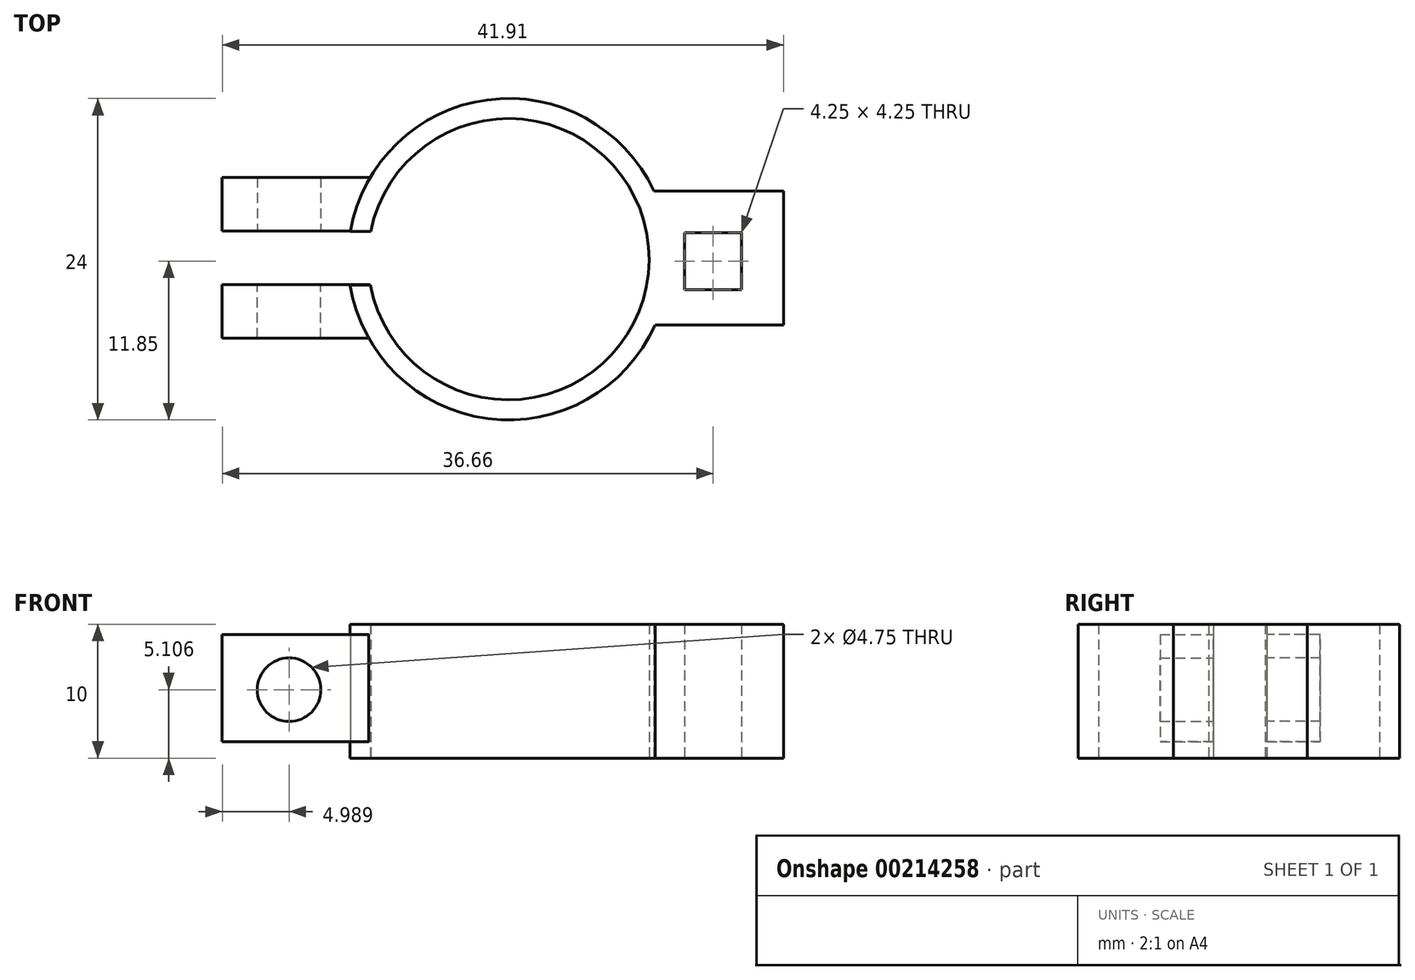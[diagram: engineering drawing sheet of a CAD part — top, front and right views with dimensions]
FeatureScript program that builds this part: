
annotation { "Feature Type Name" : "Feature", "Feature Type Description" : "" }
export const myFeature = defineFeature(function(context is Context, id is Id, definition is map)
    precondition{}
    {
        {
            var Q0;
            Q0=qCreatedBy(makeId("Top.planeOp"),FACE);
            var sketch = newSketch(context, id + "F0", { "sketchPlane" : qUnion([Q0])});
            skLineSegment(sketch, "E0.bottom", {"start": v(7.35, 1.88) * mm, "end": v(3.1, 1.88) * mm});
            skLineSegment(sketch, "E0.top", {"start": v(7.36, -2.38) * mm, "end": v(3.1, -2.38) * mm});
            skLineSegment(sketch, "E0.left", {"start": v(7.35, 1.88) * mm, "end": v(7.36, -2.37) * mm});
            skLineSegment(sketch, "E0.right", {"start": v(3.1, 1.88) * mm, "end": v(3.1, -2.38) * mm});
            skPoint(sketch, "E0.middle", {"position": v(0, 0) * mm});
            skLineSegment(sketch, "E1.bottom", {"start": v(10.48, 5) * mm, "end": v(0.48, 5) * mm});
            skLineSegment(sketch, "E1.top", {"start": v(10.48, -5) * mm, "end": v(0.48, -5) * mm});
            skLineSegment(sketch, "E1.left", {"start": v(10.48, 5) * mm, "end": v(10.48, -5) * mm});
            skLineSegment(sketch, "E1.right", {"start": v(0.48, 5) * mm, "end": v(0.48, -5) * mm});
            skCircle(sketch, "E2", {"center": v(-10.05, -0.1) * mm, "radius": 10.5 * mm});
            skPoint(sketch, "E2.first.point", {"position": v(-2, 6.7) * mm});
            skPoint(sketch, "E2.second.point", {"position": v(-17, 0) * mm});
            skPoint(sketch, "E2.second.point.positionSnap0", {"position": v(-5, 0) * mm});
            skPoint(sketch, "E2.third.point", {"position": v(-18.97, 10.9) * mm});
            skCircle(sketch, "E3", {"center": v(-10.05, -0.1) * mm, "radius": 12 * mm});
            skLineSegment(sketch, "E4", {"start": v(-8.6, -0.1) * mm, "end": v(-17, 0) * mm});
            skLineSegment(sketch, "E5.bottom", {"start": v(-22.34, -2.03) * mm, "end": v(-16.99, -2.03) * mm});
            skLineSegment(sketch, "E5.top", {"start": v(-22.34, 1.97) * mm, "end": v(-16.99, 1.97) * mm});
            skLineSegment(sketch, "E5.left", {"start": v(-22.34, -2.03) * mm, "end": v(-22.34, 1.97) * mm});
            skLineSegment(sketch, "E5.right", {"start": v(-16.99, -2.03) * mm, "end": v(-16.99, 1.97) * mm});
            skPoint(sketch, "E5.cornerSnap0", {"position": v(-19.68, 0) * mm});
            skSolve(sketch);
        }
        {
            var Q0;
            Q0=makeQuery(id+"F0.imprint","IMPRINT",FACE,{"disambiguationData":[TD([[makeQuery(id+"F0.imprint","IMPRINT",EDGE,{"derivedFrom":sQuery(id+"F0.wireOp",EDGE,"E0.bottom")}),-1.0]])]});
            var Q1;
            {var subQ0=sQuery(id+"F0.wireOp",EDGE,"E3");var subQ1=sQuery(id+"F0.wireOp",EDGE,"E1.right");var subQ2=makeQuery(id+"F0.imprint","INTERSECT",VERTEX,{"disambiguationData":[OD(0.0)],"derivedFrom":[subQ1,subQ0]});Q1=makeQuery(id+"F0.imprint","IMPRINT",FACE,{"disambiguationData":[TD([[makeQuery(id+"F0.imprint","IMPRINT",EDGE,{"disambiguationData":[TD([[subQ2,-1.0]])],"derivedFrom":subQ1}),1.0]])]});}
            var Q2;
            {var subQ0=sQuery(id+"F0.wireOp",EDGE,"E3");var subQ1=sQuery(id+"F0.wireOp",EDGE,"E1.right");var subQ2=makeQuery(id+"F0.imprint","INTERSECT",VERTEX,{"disambiguationData":[OD(1.0)],"derivedFrom":[subQ1,subQ0]});Q2=makeQuery(id+"F0.imprint","IMPRINT",FACE,{"disambiguationData":[TD([[makeQuery(id+"F0.imprint","IMPRINT",EDGE,{"disambiguationData":[TD([[subQ2,1.0]])],"derivedFrom":subQ1}),-1.0]])]});}
            var Q3;
            {var subQ0=sQuery(id+"F0.wireOp",EDGE,"E3");var subQ1=sQuery(id+"F0.wireOp",EDGE,"E1.right");var subQ2=makeQuery(id+"F0.imprint","INTERSECT",VERTEX,{"disambiguationData":[OD(0.0)],"derivedFrom":[subQ1,subQ0]});Q3=makeQuery(id+"F0.imprint","IMPRINT",FACE,{"disambiguationData":[TD([[makeQuery(id+"F0.imprint","IMPRINT",EDGE,{"disambiguationData":[TD([[subQ2,-1.0]])],"derivedFrom":subQ1}),-1.0]])]});}
            extrude(context, id + "F1", {"entities" : qUnion([Q0, Q1, Q2, Q3]), "endBound" : BoundingType.SYMMETRIC, "depth" : 10 * mm});
        }
        {
            var Q0;
            Q0=qCreatedBy(makeId("Front.planeOp"),FACE);
            var sketch = newSketch(context, id + "F2", { "sketchPlane" : qUnion([Q0])});
            skLineSegment(sketch, "E6", {"start": v(-20.43, 0.22) * mm, "end": v(-20.43, 4.22) * mm});
            skLineSegment(sketch, "E7", {"start": v(-20.43, -3.78) * mm, "end": v(-20.43, 0.22) * mm});
            skPoint(sketch, "E8", {"position": v(-25.64, 0.1) * mm});
            skLineSegment(sketch, "E9", {"start": v(-20.43, 4.22) * mm, "end": v(-31.43, 4.22) * mm});
            skLineSegment(sketch, "E10", {"start": v(-31.43, 4.22) * mm, "end": v(-31.43, -3.78) * mm});
            skLineSegment(sketch, "E11", {"start": v(-31.43, -3.78) * mm, "end": v(-20.43, -3.78) * mm});
            skLineSegment(sketch, "E12", {"start": v(-20.43, 4.22) * mm, "end": v(-31.43, -3.78) * mm});
            skLineSegment(sketch, "E13", {"start": v(-31.43, 4.22) * mm, "end": v(-20.43, -3.78) * mm});
            skCircle(sketch, "E14", {"center": v(-26.44, 0.1) * mm, "radius": 2.38 * mm});
            skSolve(sketch);
        }
        {
            var Q0;
            {var subQ0=sQuery(id+"F2.wireOp",EDGE,"E10");Q0=makeQuery(id+"F2.imprint","IMPRINT",FACE,{"disambiguationData":[TD([[makeQuery(id+"F2.imprint","IMPRINT",EDGE,{"derivedFrom":subQ0}),1.0]])]});}
            var Q1;
            {var subQ0=sQuery(id+"F2.wireOp",EDGE,"E9");Q1=makeQuery(id+"F2.imprint","IMPRINT",FACE,{"disambiguationData":[TD([[makeQuery(id+"F2.imprint","IMPRINT",EDGE,{"derivedFrom":subQ0}),1.0]])]});}
            var Q2;
            {var subQ5=sQuery(id+"F2.wireOp",EDGE,"E6");Q2=makeQuery(id+"F2.imprint","IMPRINT",FACE,{"disambiguationData":[TD([[makeQuery(id+"F2.imprint","IMPRINT",EDGE,{"derivedFrom":subQ5}),1.0]])]});}
            var Q3;
            {var subQ0=sQuery(id+"F2.wireOp",EDGE,"E11");Q3=makeQuery(id+"F2.imprint","IMPRINT",FACE,{"disambiguationData":[TD([[makeQuery(id+"F2.imprint","IMPRINT",EDGE,{"derivedFrom":subQ0}),1.0]])]});}
            extrude(context, id + "F3", {"entities" : qUnion([Q0, Q1, Q2, Q3]), "operationType" : NewBodyOperationType.ADD, "depth" : 6 * mm, "hasSecondDirection" : true, "secondDirectionOppositeDirection" : false, "secondDirectionDepth" : 2 * mm});
        }
        {
            var Q0;
            {var subQ0=sQuery(id+"F2.wireOp",EDGE,"E10");Q0=makeQuery(id+"F2.imprint","IMPRINT",FACE,{"disambiguationData":[TD([[makeQuery(id+"F2.imprint","IMPRINT",EDGE,{"derivedFrom":subQ0}),1.0]])]});}
            var Q1;
            {var subQ0=sQuery(id+"F2.wireOp",EDGE,"E9");Q1=makeQuery(id+"F2.imprint","IMPRINT",FACE,{"disambiguationData":[TD([[makeQuery(id+"F2.imprint","IMPRINT",EDGE,{"derivedFrom":subQ0}),1.0]])]});}
            var Q2;
            {var subQ5=sQuery(id+"F2.wireOp",EDGE,"E6");Q2=makeQuery(id+"F2.imprint","IMPRINT",FACE,{"disambiguationData":[TD([[makeQuery(id+"F2.imprint","IMPRINT",EDGE,{"derivedFrom":subQ5}),1.0]])]});}
            var Q3;
            {var subQ0=sQuery(id+"F2.wireOp",EDGE,"E11");Q3=makeQuery(id+"F2.imprint","IMPRINT",FACE,{"disambiguationData":[TD([[makeQuery(id+"F2.imprint","IMPRINT",EDGE,{"derivedFrom":subQ0}),1.0]])]});}
            extrude(context, id + "F4", {"entities" : qUnion([Q0, Q1, Q2, Q3]), "operationType" : NewBodyOperationType.ADD, "oppositeDirection" : true, "depth" : 6 * mm, "hasSecondDirection" : true, "secondDirectionOppositeDirection" : true, "secondDirectionDepth" : 2 * mm});
        }
    });
